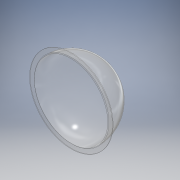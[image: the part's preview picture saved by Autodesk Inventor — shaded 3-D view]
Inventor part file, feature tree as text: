
AUTODESK INVENTOR PART (.ipt)
format: ipt  version: 2017 SP1 (Build 210196100, 196)  size: 151,552 bytes
history: native  units: mm
features: extrude x2, sketch x2, fillet x1, shell x1
ambient origin geometry x8: Origin, YZ Plane, XZ Plane, XY Plane, X Axis, Y Axis, Z Axis, Center Point
bodies: Solid1 (feature_tree)
feature tree (6):
  extrude  "Extrusion1"  Depth=4.0mm TaperAngle=0.0deg
  extrude  "Extrusion2"  Depth=225.0mm TaperAngle=0.0deg
  fillet  "Fillet1"  Radius=225.0mm
  shell  "Shell1"  Thickness=4.0mm
  sketch  "Sketch1"  dims[d0=500.0mm d1=4.0mm d2=0.0mm]
  sketch  "Sketch2"  dims[d3=450.0mm d4=225.0mm d5=0.0mm d6=225.0mm d7=4.0mm]
